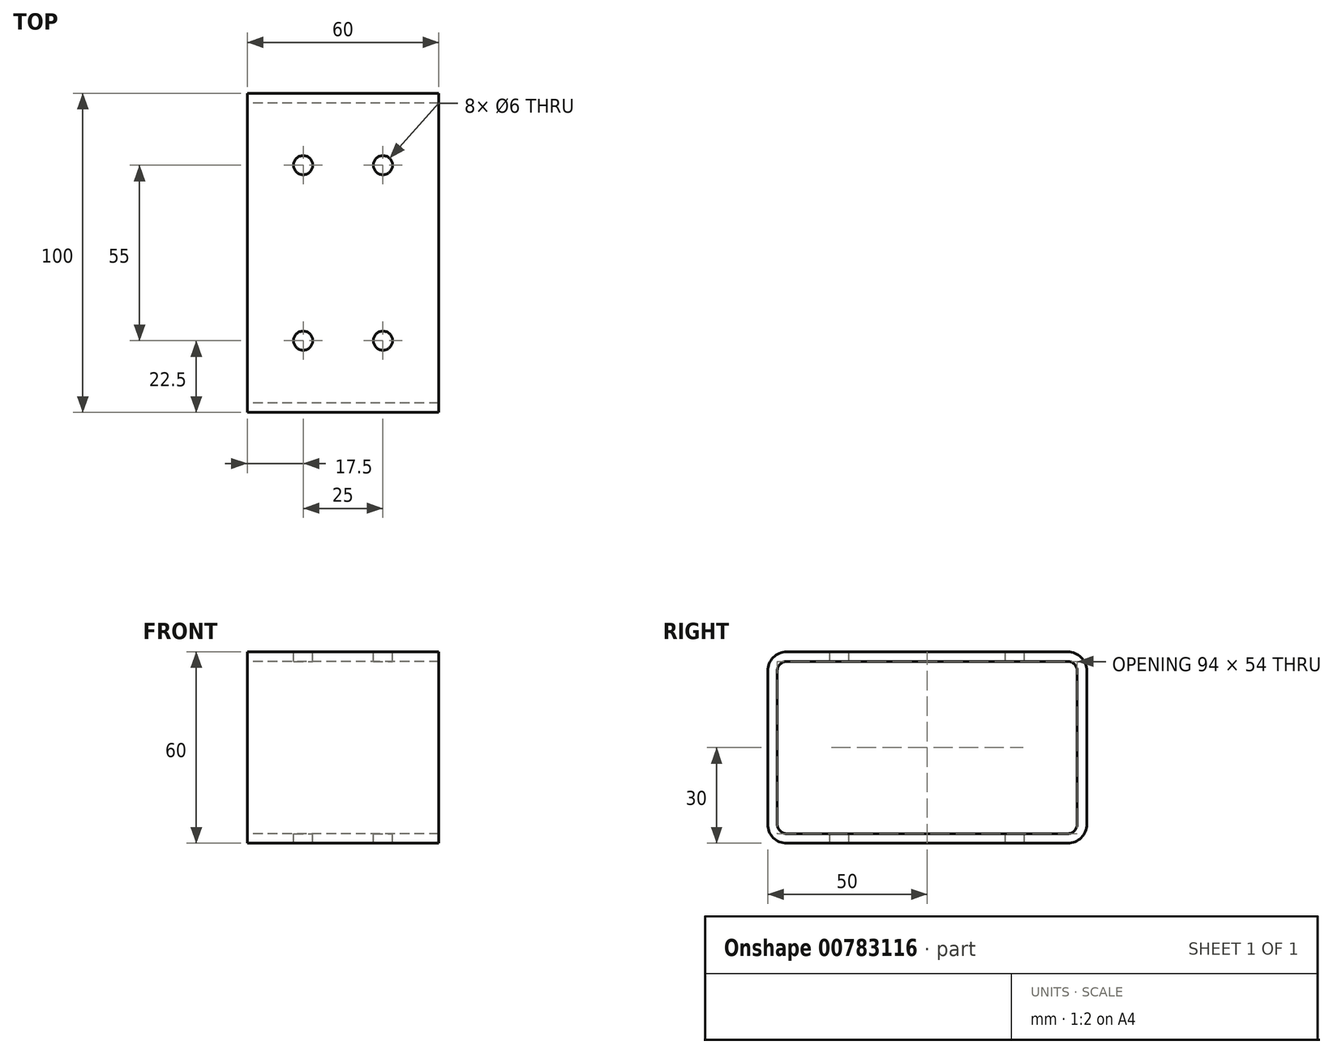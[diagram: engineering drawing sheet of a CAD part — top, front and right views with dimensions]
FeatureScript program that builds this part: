
annotation { "Feature Type Name" : "Feature", "Feature Type Description" : "" }
export const myFeature = defineFeature(function(context is Context, id is Id, definition is map)
    precondition{}
    {
        {
            var Q0;
            Q0=qCreatedBy(makeId("Right.planeOp"),FACE);
            var sketch = newSketch(context, id + "F0", { "sketchPlane" : qUnion([Q0])});
            skLineSegment(sketch, "E0.bottom", {"start": v(-6, 0) * mm, "end": v(-94, 0) * mm});
            skLineSegment(sketch, "E0.top", {"start": v(-6, 60) * mm, "end": v(-94, 60) * mm});
            skLineSegment(sketch, "E0.left", {"start": v(0, 6) * mm, "end": v(0, 54) * mm});
            skLineSegment(sketch, "E0.right", {"start": v(-100, 6) * mm, "end": v(-100, 54) * mm});
            skPoint(sketch, "E1.visualSharp", {"position": v(-100, 60) * mm});
            skArc(sketch, "E1.filletArc", {"start": v(-94, 60) * mm, "mid": v(-98.24, 58.24) * mm, "end": v(-100, 54) * mm});
            skPoint(sketch, "E2.visualSharp", {"position": v(-100, 0) * mm});
            skArc(sketch, "E2.filletArc", {"start": v(-100, 6) * mm, "mid": v(-98.24, 1.76) * mm, "end": v(-94, 0) * mm});
            skPoint(sketch, "E3.visualSharp", {"position": v(0, 0) * mm});
            skArc(sketch, "E3.filletArc", {"start": v(-6, 0) * mm, "mid": v(-1.76, 1.76) * mm, "end": v(0, 6) * mm});
            skPoint(sketch, "E4.visualSharp", {"position": v(0, 60) * mm});
            skArc(sketch, "E4.filletArc", {"start": v(0, 54) * mm, "mid": v(-1.76, 58.24) * mm, "end": v(-6, 60) * mm});
            skArc(sketch, "E5.0", {"start": v(-97, 6) * mm, "mid": v(-96.12, 3.88) * mm, "end": v(-94, 3) * mm});
            skLineSegment(sketch, "E5.1", {"start": v(-6, 3) * mm, "end": v(-94, 3) * mm});
            skLineSegment(sketch, "E5.2", {"start": v(-97, 6) * mm, "end": v(-97, 54) * mm});
            skArc(sketch, "E5.3", {"start": v(-6, 3) * mm, "mid": v(-3.88, 3.88) * mm, "end": v(-3, 6) * mm});
            skArc(sketch, "E5.4", {"start": v(-94, 57) * mm, "mid": v(-96.12, 56.12) * mm, "end": v(-97, 54) * mm});
            skLineSegment(sketch, "E5.5", {"start": v(-6, 57) * mm, "end": v(-94, 57) * mm});
            skArc(sketch, "E5.6", {"start": v(-3, 54) * mm, "mid": v(-3.88, 56.12) * mm, "end": v(-6, 57) * mm});
            skLineSegment(sketch, "E5.7", {"start": v(-3, 6) * mm, "end": v(-3, 54) * mm});
            skSolve(sketch);
        }
        {
            var Q0;
            Q0=makeQuery(id+"F0.imprint","IMPRINT",FACE,{"disambiguationData":[TD([[makeQuery(id+"F0.imprint","IMPRINT",EDGE,{"derivedFrom":sQuery(id+"F0.wireOp",EDGE,"E0.bottom")}),-1.0]])]});
            extrude(context, id + "F1", {"entities" : qUnion([Q0]), "depth" : 60 * mm, "offsetDistance" : 25 * mm});
        }
        {
            var Q0;
            Q0=makeQuery(id+"F1.opExtrude","SWEPT_FACE",FACE,{"disambiguationData":[OSD([sQuery(id+"F0.wireOp",EDGE,"E0.top")])]});
            var sketch = newSketch(context, id + "F2", { "sketchPlane" : qUnion([Q0])});
            skCircle(sketch, "E6", {"center": v(17.5, -22.5) * mm, "radius": 3.95 * mm});
            skCircle(sketch, "E7", {"center": v(42.5, -22.5) * mm, "radius": 1.65 * mm});
            skCircle(sketch, "E8", {"center": v(17.5, -77.5) * mm, "radius": 2.96 * mm});
            skCircle(sketch, "E9", {"center": v(42.5, -77.5) * mm, "radius": 3.17 * mm});
            skSolve(sketch);
        }
        {
            var Q0;
            Q0=sQuery(id+"F2.wireOp",VERTEX,"E6.center");
            var Q1;
            Q1=sQuery(id+"F2.wireOp",VERTEX,"E7.center");
            var Q2;
            Q2=sQuery(id+"F2.wireOp",VERTEX,"E8.center");
            var Q3;
            Q3=sQuery(id+"F2.wireOp",VERTEX,"E9.center");
            var Q4;
            Q4=makeQuery(id+"F1.opExtrude","SWEPT_BODY",BODY,{"disambiguationData":[OSD([sQuery(id+"F0.wireOp",EDGE,"E0.bottom"),sQuery(id+"F0.wireOp",EDGE,"E0.top"),sQuery(id+"F0.wireOp",EDGE,"E0.left"),sQuery(id+"F0.wireOp",EDGE,"E0.right"),sQuery(id+"F0.wireOp",EDGE,"E1.filletArc"),sQuery(id+"F0.wireOp",EDGE,"E2.filletArc"),sQuery(id+"F0.wireOp",EDGE,"E3.filletArc"),sQuery(id+"F0.wireOp",EDGE,"E4.filletArc"),sQuery(id+"F0.wireOp",EDGE,"E5.0"),sQuery(id+"F0.wireOp",EDGE,"E5.1"),sQuery(id+"F0.wireOp",EDGE,"E5.2"),sQuery(id+"F0.wireOp",EDGE,"E5.3"),sQuery(id+"F0.wireOp",EDGE,"E5.4"),sQuery(id+"F0.wireOp",EDGE,"E5.5"),sQuery(id+"F0.wireOp",EDGE,"E5.6"),sQuery(id+"F0.wireOp",EDGE,"E5.7")])]});
            hole(context, id + "F3", {"style" : HoleStyle.SIMPLE, "endStyle" : HoleEndStyle.THROUGH, "holeDiameter" : 6 * mm, "majorDiameter" : 5 * mm, "isTappedThrough" : true, "tappedDepth" : 12 * mm, "tapClearance" : 3, "locations" : qUnion([Q0, Q1, Q2, Q3]), "scope" : qUnion([Q4])});
        }
    });
